# Revit family: Domotics-DomesticRanges-GEWISS-CHORUS_POWER-SOCKET-OUTLET_CHINA
name_source: partatom
category: Apparecchi elettrici
revit_build: Autodesk Revit 2016 (Build: 20161004_0715(x64)
units: mm (PartAtom-declared; Revit-internal decimal feet)

## family parameters
Condiviso = Sì
Host = Superficie
Mantenere orientamento annotazione = Sì
Punto di calcolo locali = Sì
Quota connettore circolare = Usa diametro
Taglio con vuoti quando caricato = Sì
Tipo di parte = Normale

## types (6) — shared parameters
Carico apparente = 0 VA
Catalogue = DOMOTICS
Catalogue Range = CHORUS - DOMESTIC RANGE
Electrocod = 0131
Finitura = GEWISS TITANIO
IDF = 14ab5456-2b76-4947-be2c-9dddb89139cf
IDT = aaf2509b-0dc0-40c7-94b0-3c64b419fe1f
Immagine tipo = GW14392.jpg
N. poli = 1
Produttore = GEWISS S.p.A.
Prospetto di default = 1219 mm
TIPO_ = Chorus Prese Australia_GENERICO : GW14307 Presa 2M 2P+T 15A standard Australiano titanio
TXT ELETTRICO = 16
Technical sheet = https://www.gewiss.com
URL = https://www.gewiss.com
Version file RFA = 19.0
Volt = 230 V

## per-type parameters (varying)
| type | Descrizione | EAN code | Modello |
| GW10391 - CHINESE STD 2P+E 10A CH/WT | CHINESE STD 2P+E 10A CH/WT | 8011564445017 | GW10391 |
| GW12391 - CHINESE STD 2P+E 10A CH/BK | CHINESE STD 2P+E 10A CH/BK | 8011564445024 | GW12391 |
| GW14392 - CHINESE STD 2P+E 16A CH/TI | CHINESE STD 2P+E 16A CH/TI | 8011564445062 | GW14392 |
| GW12392 - CHINESE STD 2P+E 16A CH/BK | CHINESE STD 2P+E 16A CH/BK | 8011564445055 | GW12392 |
| GW10392 - CHINESE STD 2P+E 16A CH/WT | CHINESE STD 2P+E 16A CH/WT | 8011564445048 | GW10392 |
| GW14391 - CHINESE STD 2P+E 10A CH/TI | CHINESE STD 2P+E 10A CH/TI | 8011564445031 | GW14391 |

## geometry (parser evidence)
native form markers: Sweep x2
no freeform markers — native parametric forms only
